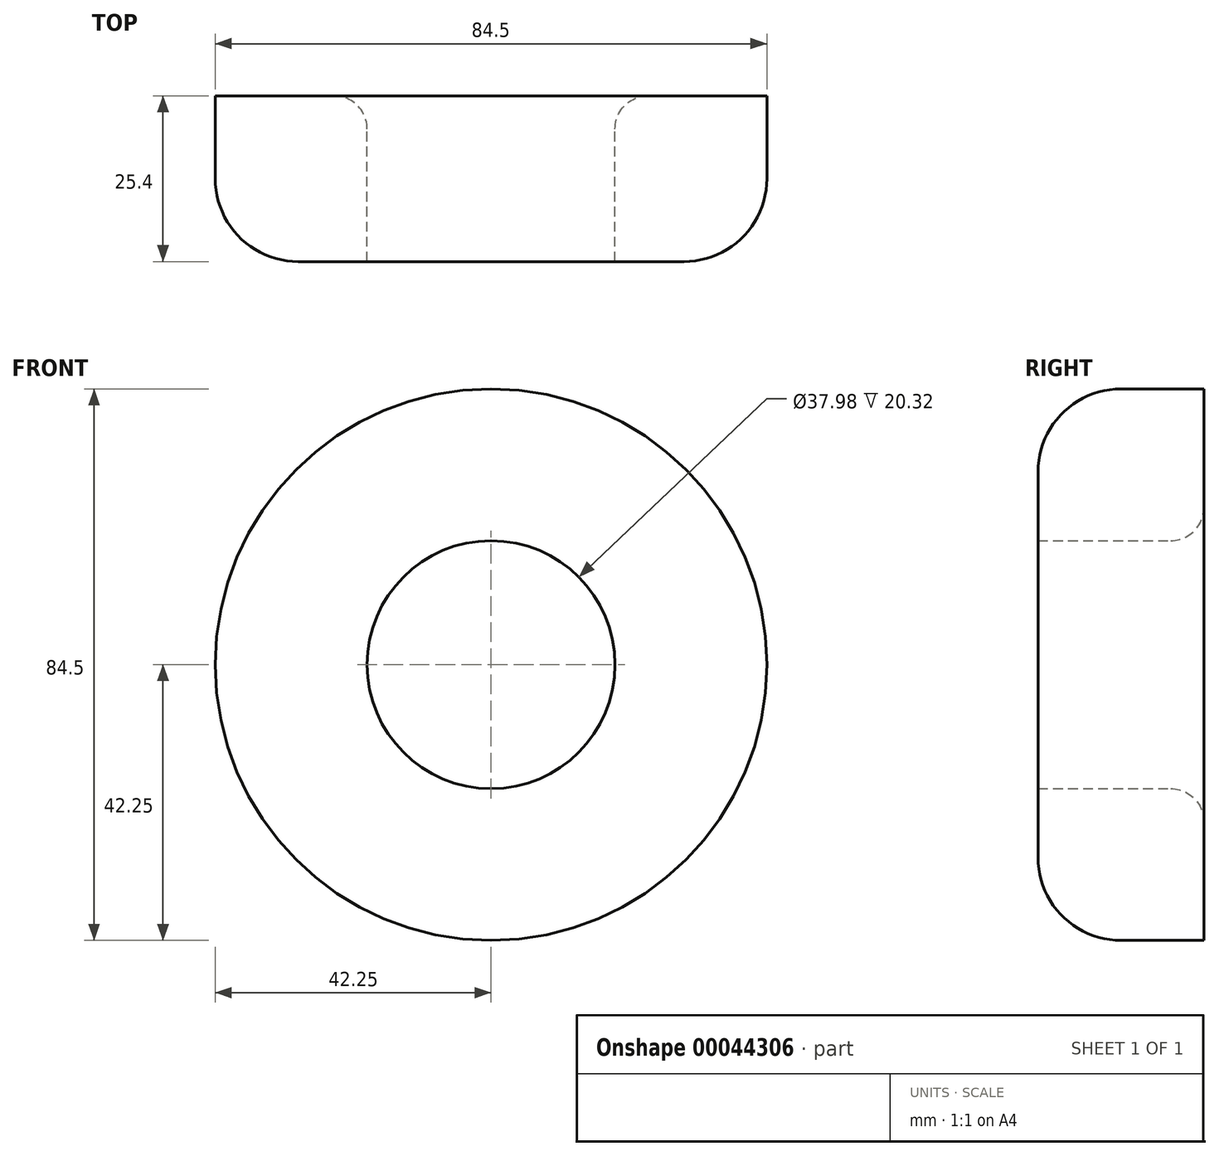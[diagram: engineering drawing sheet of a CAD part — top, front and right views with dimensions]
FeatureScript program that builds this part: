
annotation { "Feature Type Name" : "Feature", "Feature Type Description" : "" }
export const myFeature = defineFeature(function(context is Context, id is Id, definition is map)
    precondition{}
    {
        {
            var Q0;
            Q0=qCreatedBy(makeId("Front.planeOp"),FACE);
            var sketch = newSketch(context, id + "F0", { "sketchPlane" : qUnion([Q0])});
            skCircle(sketch, "E0", {"center": v(0, 0) * mm, "radius": 18.99 * mm});
            skCircle(sketch, "E1", {"center": v(0, 0) * mm, "radius": 42.25 * mm});
            skSolve(sketch);
        }
        {
            var Q0;
            Q0 = qSketchRegion(id + "F0", true);
            extrude(context, id + "F1", {"entities" : qUnion([Q0]), "depth" : 25.4 * mm});
        }
        {
            var Q0;
            Q0=makeQuery(id+"F1.opExtrude","CAP_EDGE",EDGE,{"disambiguationData":[OSD([sQuery(id+"F0.wireOp",EDGE,"E1")])],"isStart":false});
            fillet(context, id + "F2", {"entities" : qUnion([Q0]), "radius" : 12.7 * mm, "tangentPropagation" : true, "allowEdgeOverflow" : false});
        }
        {
            var Q0;
            Q0=makeQuery(id+"F1.opExtrude","CAP_EDGE",EDGE,{"disambiguationData":[OSD([sQuery(id+"F0.wireOp",EDGE,"E0")])],"isStart":true});
            fillet(context, id + "F3", {"entities" : qUnion([Q0]), "radius" : 5.08 * mm, "tangentPropagation" : true, "allowEdgeOverflow" : false});
        }
    });
